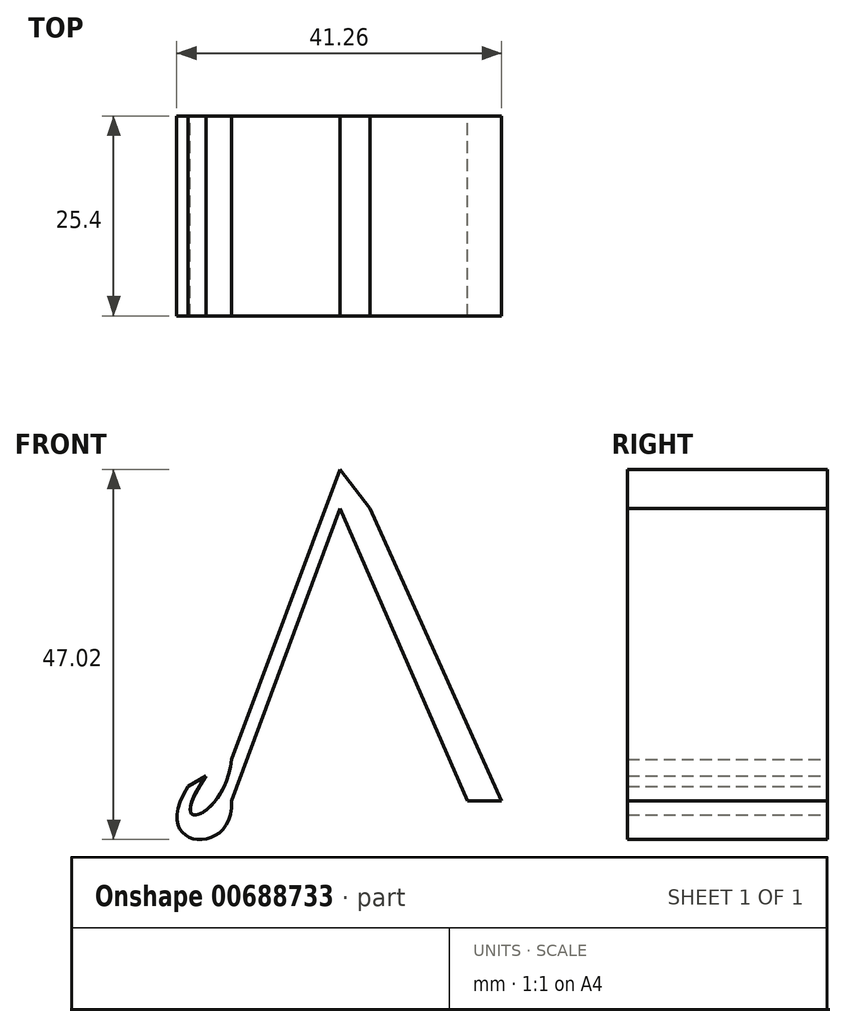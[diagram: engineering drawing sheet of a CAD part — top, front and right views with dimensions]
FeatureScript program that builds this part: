
annotation { "Feature Type Name" : "Feature", "Feature Type Description" : "" }
export const myFeature = defineFeature(function(context is Context, id is Id, definition is map)
    precondition{}
    {
        {
            var Q0;
            Q0=qCreatedBy(makeId("Front.planeOp"),FACE);
            var sketch = newSketch(context, id + "F0", { "sketchPlane" : qUnion([Q0])});
            skFitSpline(sketch, "E0", {"points": [v(-34.28, 0) * mm, v(-39.81, 1.81) * mm], "startDerivative": vector(1.15, -22.06) * mm, "endDerivative": vector(16.04, 24.06) * mm});
            skLineSegment(sketch, "E1", {"start": v(-34.28, 0) * mm, "end": v(-20.53, 37.14) * mm});
            skLineSegment(sketch, "E2", {"start": v(-20.53, 37.14) * mm, "end": v(-4.3, 0) * mm});
            skLineSegment(sketch, "E3", {"start": v(-4.3, 0) * mm, "end": v(0, 0) * mm});
            skLineSegment(sketch, "E4", {"start": v(0, 0) * mm, "end": v(-16.7, 37.14) * mm});
            skLineSegment(sketch, "E5", {"start": v(-16.7, 37.14) * mm, "end": v(-20.53, 42.1) * mm});
            skLineSegment(sketch, "E6", {"start": v(-20.53, 42.1) * mm, "end": v(-34.28, 5.25) * mm});
            skFitSpline(sketch, "E7", {"points": [v(-34.28, 5.25) * mm, v(-37.52, 3.15) * mm], "startDerivative": vector(-2.56, -22.7) * mm, "endDerivative": vector(17.08, 24.27) * mm});
            skLineSegment(sketch, "E8", {"start": v(-37.52, 3.15) * mm, "end": v(-39.81, 1.81) * mm});
            skSolve(sketch);
        }
        {
            var Q0;
            Q0=makeQuery(id+"F0.imprint","IMPRINT",FACE,{"disambiguationData":[TD([[makeQuery(id+"F0.imprint","IMPRINT",EDGE,{"derivedFrom":sQuery(id+"F0.wireOp",EDGE,"E0")}),-1.0]])]});
            extrude(context, id + "F1", {"entities" : qUnion([Q0]), "depth" : 25.4 * mm, "offsetDistance" : 25.4 * mm});
        }
    });
